# Revit family: Sanext_Фильтр_механической_очистки_Косой
name_source: partatom
category: Арматура трубопроводов
revit_build: Autodesk Revit 2017 (Build: 20171027_0315(x64)
units: mm (PartAtom-declared; Revit-internal decimal feet)

## family parameters
Всегда вертикально = Да
На основе рабочей плоскости = Нет
Общий = Нет
При загрузке вырезать с полостями = Нет
Размер круглого соединителя = Использовать радиус
Тип детали = Вставляется

## types (6) — shared parameters
ADSK_Единица измерения = шт
ADSK_Завод-изготовитель = ООО САНЕКСТ ПРО
ADSK_Материал наименование = DZR латунь
URL = http://sanext.ru
Группа модели = Фильтр
Изготовитель = ООО САНЕКСТ ПРО
Материал стальной части = DZR латунь
Рабочее давление = 0.0 кПа
Разработчик = ООО ПРОРУБИМ
Разработчик (телефон) = +7(495)649-85-43
Разработчик модели (URL) = http://prorubim.com
zero-valued in all types: ADSK_Масса

## per-type parameters (varying)
| type | ADSK_Код изделия | ADSK_Наименование | D | H | L | R | z | Гайка | Описание |
| Ду15 | 8911 | Фильтр механической очистки косой, Ду 15 с внутренней резьбой | 15 мм | 36 мм | 53 мм | 8 мм | 1 | 15 мм | Фильтр механической очистки косой, Ду 15 с внутренней резьбой |
| Ду20 | 8912 | Фильтр механической очистки косой, Ду 20 с внутренней резьбой | 20 мм | 43 мм | 65 мм | 10 мм | 0 | 20 мм | Фильтр механической очистки косой, Ду 20 с внутренней резьбой |
| Ду25 | 8913 | Фильтр механической очистки косой, Ду 25 с внутренней резьбой | 25 мм | 54 мм | 77 мм | 13 мм | 0 | 25 мм | Фильтр механической очистки косой, Ду 25 с внутренней резьбой |
| Ду32 | 8914 | Фильтр механической очистки косой, Ду 32 с внутренней резьбой | 32 мм | 65 мм | 91 мм | 16 мм | 0 | 32 мм | Фильтр механической очистки косой, Ду 32 с внутренней резьбой |
| Ду40 | 8915 | Фильтр механической очистки косой, Ду 40 с внутренней резьбой | 40 мм | 78 мм | 111 мм | 20 мм | 0 | 40 мм | Фильтр механической очистки косой, Ду 40 с внутренней резьбой |
| Ду50 | 8916 | Фильтр механической очистки косой, Ду 50 с внутренней резьбой | 50 мм | 90 мм | 135 мм | 25 мм | 0 | 50 мм | Фильтр механической очистки косой, Ду 50 с внутренней резьбой |
